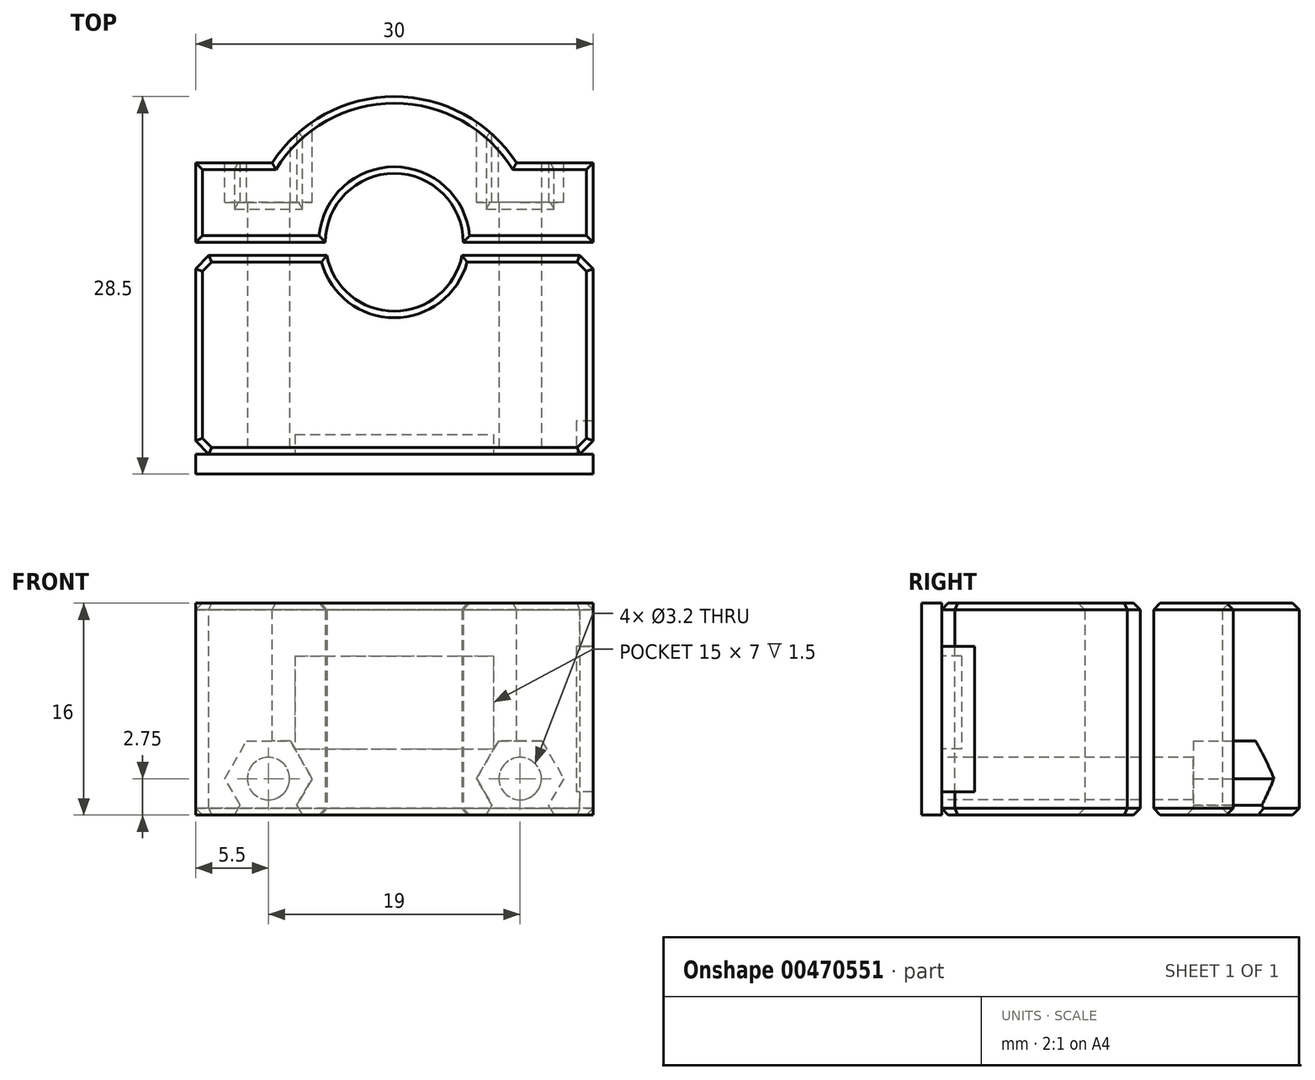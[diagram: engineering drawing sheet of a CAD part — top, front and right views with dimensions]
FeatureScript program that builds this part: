
annotation { "Feature Type Name" : "Feature", "Feature Type Description" : "" }
export const myFeature = defineFeature(function(context is Context, id is Id, definition is map)
    precondition{}
    {
        {
            var Q0;
            Q0=qCreatedBy(makeId("Top.planeOp"),FACE);
            var sketch = newSketch(context, id + "F0", { "sketchPlane" : qUnion([Q0])});
            skCircle(sketch, "E0", {"center": v(0, 0) * mm, "radius": 5.2 * mm});
            skSolve(sketch);
        }
        {
            var Q0;
            Q0=makeQuery(id+"F0.imprint","IMPRINT",FACE,{"disambiguationData":[TD([[makeQuery(id+"F0.imprint","IMPRINT",EDGE,{"derivedFrom":sQuery(id+"F0.wireOp",EDGE,"E0")}),1.0]])]});
            extrude(context, id + "F1", {"entities" : qUnion([Q0]), "depth" : 25 * mm, "hasSecondDirection" : true, "secondDirectionOppositeDirection" : true, "secondDirectionDepth" : 25 * mm});
        }
        {
            var Q0;
            Q0=qCreatedBy(makeId("Front.planeOp"),FACE);
            cPlane(context, id + "F2", {"entities" : qUnion([Q0]), "cplaneType" : CPlaneType.OFFSET, "offset" : 16 * mm, "width" : 150 * mm, "height" : 150 * mm});
        }
        {
            var Q0;
            Q0=qCreatedBy(id+"F2.planeOp",FACE);
            var sketch = newSketch(context, id + "F3", { "sketchPlane" : qUnion([Q0])});
            skPoint(sketch, "E1", {"position": v(-9.5, 0) * mm});
            skPoint(sketch, "E2", {"position": v(9.5, 0) * mm});
            skLineSegment(sketch, "E3.bottom", {"start": v(-15, -2.75) * mm, "end": v(15, -2.75) * mm});
            skLineSegment(sketch, "E3.top", {"start": v(-15, 13.25) * mm, "end": v(15, 13.25) * mm});
            skLineSegment(sketch, "E3.left", {"start": v(-15, -2.75) * mm, "end": v(-15, 13.25) * mm});
            skLineSegment(sketch, "E3.right", {"start": v(15, -2.75) * mm, "end": v(15, 13.25) * mm});
            skSolve(sketch);
        }
        {
            var Q0;
            Q0=makeQuery(id+"F3.imprint","IMPRINT",FACE,{"disambiguationData":[TD([[makeQuery(id+"F3.imprint","IMPRINT",EDGE,{"derivedFrom":sQuery(id+"F3.wireOp",EDGE,"E3.bottom")}),1.0]])]});
            extrude(context, id + "F4", {"entities" : qUnion([Q0]), "oppositeDirection" : true, "depth" : 27 * mm});
        }
        {
            var Q0;
            Q0=makeQuery(id+"F3.imprint","IMPRINT",FACE,{"disambiguationData":[TD([[makeQuery(id+"F3.imprint","IMPRINT",EDGE,{"derivedFrom":sQuery(id+"F3.wireOp",EDGE,"E3.bottom")}),1.0]])]});
            extrude(context, id + "F5", {"entities" : qUnion([Q0]), "depth" : 1.5 * mm});
        }
        {
            var Q0;
            Q0=sQuery(id+"F3.wireOp",VERTEX,"E1");
            var Q1;
            Q1=sQuery(id+"F3.wireOp",VERTEX,"E2");
            var Q2;
            Q2=makeQuery(id+"F4.opExtrude","SWEPT_BODY",BODY,{"disambiguationData":[OSD([sQuery(id+"F3.wireOp",EDGE,"E3.bottom"),sQuery(id+"F3.wireOp",EDGE,"E3.top"),sQuery(id+"F3.wireOp",EDGE,"E3.left"),sQuery(id+"F3.wireOp",EDGE,"E3.right")])]});
            hole(context, id + "F6", {"style" : HoleStyle.SIMPLE, "endStyle" : HoleEndStyle.BLIND, "holeDiameter" : 3.2 * mm, "holeDepth" : (25 - 1.5) * mm, "isTappedThrough" : true, "tappedDepth" : 15 * mm, "tapClearance" : 0, "locations" : qUnion([Q0, Q1]), "scope" : qUnion([Q2])});
        }
        {
            var Q0;
            Q0=makeQuery(id+"F4.opExtrude","CAP_FACE",FACE,{"disambiguationData":[OSD([sQuery(id+"F3.wireOp",EDGE,"E3.bottom"),sQuery(id+"F3.wireOp",EDGE,"E3.top"),sQuery(id+"F3.wireOp",EDGE,"E3.left"),sQuery(id+"F3.wireOp",EDGE,"E3.right")])],"isStart":false});
            var sketch = newSketch(context, id + "F7", { "sketchPlane" : qUnion([Q0])});
            skCircle(sketch, "E4.cCircle", {"center": v(-9.5, 0) * mm, "radius": 2.85 * mm, "construction": true});
            skLineSegment(sketch, "E4.0", {"start": v(-6.2, 0) * mm, "end": v(-7.85, -2.85) * mm});
            skLineSegment(sketch, "E4.1", {"start": v(-7.85, -2.85) * mm, "end": v(-11.15, -2.85) * mm});
            skLineSegment(sketch, "E4.2", {"start": v(-11.15, -2.85) * mm, "end": v(-12.8, 0) * mm});
            skLineSegment(sketch, "E4.3", {"start": v(-12.8, 0) * mm, "end": v(-11.15, 2.85) * mm});
            skLineSegment(sketch, "E4.4", {"start": v(-11.15, 2.85) * mm, "end": v(-7.85, 2.85) * mm});
            skLineSegment(sketch, "E4.5", {"start": v(-7.85, 2.85) * mm, "end": v(-6.2, 0) * mm});
            skPoint(sketch, "E4.0.midPoint", {"position": v(-7.03, -1.43) * mm});
            skLineSegment(sketch, "E5.MirrorCS", {"start": v(11.15, 2.85) * mm, "end": v(7.85, 2.85) * mm});
            skLineSegment(sketch, "E6.MirrorCS", {"start": v(6.2, 0) * mm, "end": v(7.85, -2.85) * mm});
            skLineSegment(sketch, "E7.MirrorCS", {"start": v(7.85, 2.85) * mm, "end": v(6.2, 0) * mm});
            skLineSegment(sketch, "E8.MirrorCS", {"start": v(12.8, 0) * mm, "end": v(11.15, 2.85) * mm});
            skLineSegment(sketch, "E9.MirrorCS", {"start": v(11.15, -2.85) * mm, "end": v(12.8, 0) * mm});
            skLineSegment(sketch, "E10.MirrorCS", {"start": v(7.85, -2.85) * mm, "end": v(11.15, -2.85) * mm});
            skCircle(sketch, "E11.MirrorC", {"center": v(9.5, 0) * mm, "radius": 2.85 * mm, "construction": true});
            skPoint(sketch, "E12.MirrorP", {"position": v(7.03, -1.43) * mm});
            skSolve(sketch);
        }
        {
            var Q0;
            Q0=makeQuery(id+"F7.imprint","IMPRINT",FACE,{"disambiguationData":[TD([[makeQuery(id+"F7.imprint","IMPRINT",EDGE,{"derivedFrom":sQuery(id+"F7.wireOp",EDGE,"E4.0")}),-1.0]])]});
            var Q1;
            Q1=makeQuery(id+"F7.imprint","IMPRINT",FACE,{"disambiguationData":[TD([[makeQuery(id+"F7.imprint","IMPRINT",EDGE,{"derivedFrom":sQuery(id+"F7.wireOp",EDGE,"E5.MirrorCS")}),1.0]])]});
            var Q2;
            {var subQ0=sQuery(id+"F7.wireOp",EDGE,"E4.3");Q2=makeQuery(id+"F7.imprint","IMPRINT",FACE,{"disambiguationData":[TD([[makeQuery(id+"F7.imprint","IMPRINT",EDGE,{"derivedFrom":subQ0}),-1.0]])]});}
            extrude(context, id + "F8", {"entities" : qUnion([Q0, Q1, Q2]), "operationType" : NewBodyOperationType.REMOVE, "oppositeDirection" : true, "depth" : 8 * mm});
        }
        {
            var Q0;
            Q0=makeQuery(id+"F4.opExtrude","SWEPT_FACE",FACE,{"disambiguationData":[OSD([sQuery(id+"F3.wireOp",EDGE,"E3.top")])]});
            var sketch = newSketch(context, id + "F9", { "sketchPlane" : qUnion([Q0])});
            skArc(sketch, "E13.0", {"start": v(9.22, 6) * mm, "mid": v(0, 11) * mm, "end": v(-9.22, 6) * mm});
            skLineSegment(sketch, "E14", {"start": v(-15, 6) * mm, "end": v(-9.22, 6) * mm});
            skPoint(sketch, "E15.orphan", {"position": v(15, 0) * mm});
            skPoint(sketch, "E16.end.orphan", {"position": v(-15, 0) * mm});
            skLineSegment(sketch, "E17.MirrorCS", {"start": v(15, 6) * mm, "end": v(9.22, 6) * mm});
            skSolve(sketch);
        }
        {
            var Q0;
            {var subQ0=sQuery(id+"F9.wireOp",EDGE,"E14");Q0=makeQuery(id+"F9.imprint","IMPRINT",FACE,{"disambiguationData":[TD([[makeQuery(id+"F9.imprint","IMPRINT",EDGE,{"derivedFrom":subQ0}),1.0]])]});}
            var Q1;
            {var subQ0=sQuery(id+"F9.wireOp",EDGE,"E17.MirrorCS");Q1=makeQuery(id+"F9.imprint","IMPRINT",FACE,{"disambiguationData":[TD([[makeQuery(id+"F9.imprint","IMPRINT",EDGE,{"derivedFrom":subQ0}),-1.0]])]});}
            extrude(context, id + "F10", {"entities" : qUnion([Q0, Q1]), "operationType" : NewBodyOperationType.REMOVE, "oppositeDirection" : true, "depth" : 25 * mm});
        }
        {
            var Q0;
            Q0=makeQuery(id+"F4.opExtrude","SWEPT_FACE",FACE,{"disambiguationData":[OSD([sQuery(id+"F3.wireOp",EDGE,"E3.top")])]});
            var sketch = newSketch(context, id + "F11", { "sketchPlane" : qUnion([Q0])});
            skLineSegment(sketch, "E18.bottom", {"start": v(-15.68, 0) * mm, "end": v(17.28, 0) * mm});
            skLineSegment(sketch, "E18.top", {"start": v(-15.68, -1) * mm, "end": v(17.28, -1) * mm});
            skLineSegment(sketch, "E18.left", {"start": v(-15.68, 0) * mm, "end": v(-15.68, -1) * mm});
            skLineSegment(sketch, "E18.right", {"start": v(17.28, 0) * mm, "end": v(17.28, -1) * mm});
            skSolve(sketch);
        }
        {
            var Q0;
            {var subQ0=sQuery(id+"F11.wireOp",EDGE,"E18.bottom");var subQ1=sQuery(id+"F3.wireOp",EDGE,"E3.top");var subQ2=makeQuery(id+"F4.opExtrude","SWEPT_EDGE",EDGE,{"disambiguationData":[OSD([subQ1,sQuery(id+"F3.wireOp",EDGE,"E3.left")])]});var subQ3=makeQuery(id+"F11.imprint","INTERSECT",VERTEX,{"derivedFrom":[subQ2,subQ0]});Q0=makeQuery(id+"F11.imprint","IMPRINT",FACE,{"disambiguationData":[TD([[makeQuery(id+"F11.imprint","IMPRINT",EDGE,{"disambiguationData":[TD([[subQ3,-1.0]])],"derivedFrom":subQ0}),-1.0]])]});}
            extrude(context, id + "F12", {"entities" : qUnion([Q0]), "operationType" : NewBodyOperationType.REMOVE, "oppositeDirection" : true, "depth" : 25 * mm});
        }
        {
            var Q0;
            Q0=makeQuery(id+"F3.imprint","IMPRINT",FACE,{"disambiguationData":[TD([[makeQuery(id+"F3.imprint","IMPRINT",EDGE,{"derivedFrom":sQuery(id+"F3.wireOp",EDGE,"E3.bottom")}),1.0]])]});
            var sketch = newSketch(context, id + "F13", { "sketchPlane" : qUnion([Q0])});
            skLineSegment(sketch, "E19.bottom", {"start": v(-7.5, 9.25) * mm, "end": v(7.5, 9.25) * mm});
            skLineSegment(sketch, "E19.top", {"start": v(-7.5, 2.25) * mm, "end": v(7.5, 2.25) * mm});
            skLineSegment(sketch, "E19.left", {"start": v(-7.5, 9.25) * mm, "end": v(-7.5, 2.25) * mm});
            skLineSegment(sketch, "E19.right", {"start": v(7.5, 9.25) * mm, "end": v(7.5, 2.25) * mm});
            skSolve(sketch);
        }
        {
            var Q0;
            Q0=makeQuery(id+"F13.imprint","IMPRINT",FACE,{"disambiguationData":[TD([[makeQuery(id+"F13.imprint","IMPRINT",EDGE,{"derivedFrom":sQuery(id+"F13.wireOp",EDGE,"E19.bottom")}),-1.0]])]});
            extrude(context, id + "F14", {"entities" : qUnion([Q0]), "operationType" : NewBodyOperationType.REMOVE, "oppositeDirection" : true, "depth" : 1.5 * mm});
        }
        {
            var Q0;
            Q0=makeQuery(id+"F3.imprint","IMPRINT",FACE,{"disambiguationData":[TD([[makeQuery(id+"F3.imprint","IMPRINT",EDGE,{"derivedFrom":sQuery(id+"F3.wireOp",EDGE,"E3.bottom")}),1.0]])]});
            var sketch = newSketch(context, id + "F15", { "sketchPlane" : qUnion([Q0])});
            skLineSegment(sketch, "E20.bottom", {"start": v(18.98, 10) * mm, "end": v(13.75, 10) * mm});
            skLineSegment(sketch, "E20.top", {"start": v(18.98, -1) * mm, "end": v(13.75, -1) * mm});
            skLineSegment(sketch, "E20.left", {"start": v(18.98, 10) * mm, "end": v(18.98, -1) * mm});
            skLineSegment(sketch, "E20.right", {"start": v(13.75, 10) * mm, "end": v(13.75, -1) * mm});
            skSolve(sketch);
        }
        {
            var Q0;
            {var subQ0=sQuery(id+"F15.wireOp",EDGE,"E20.right");Q0=makeQuery(id+"F15.imprint","IMPRINT",FACE,{"disambiguationData":[TD([[makeQuery(id+"F15.imprint","IMPRINT",EDGE,{"derivedFrom":subQ0}),1.0]])]});}
            extrude(context, id + "F16", {"entities" : qUnion([Q0]), "operationType" : NewBodyOperationType.REMOVE, "oppositeDirection" : true, "depth" : 2.5 * mm});
        }
        {
            var Q0;
            Q0=makeQuery(id+"F1.opExtrude","SWEPT_BODY",BODY,{"disambiguationData":[OSD([sQuery(id+"F0.wireOp",EDGE,"E0")])]});
            var Q1;
            Q1=makeQuery(id+"F12.boolean.opBoolean","SPLIT",BODY,{"disambiguationData":[OD(1.0)],"derivedFrom":makeQuery(id+"F4.opExtrude","SWEPT_BODY",BODY,{"disambiguationData":[OSD([sQuery(id+"F3.wireOp",EDGE,"E3.bottom"),sQuery(id+"F3.wireOp",EDGE,"E3.top"),sQuery(id+"F3.wireOp",EDGE,"E3.left"),sQuery(id+"F3.wireOp",EDGE,"E3.right")])]})});
            var Q2;
            Q2=makeQuery(id+"F12.boolean.opBoolean","SPLIT",BODY,{"disambiguationData":[OD(0.0)],"derivedFrom":makeQuery(id+"F4.opExtrude","SWEPT_BODY",BODY,{"disambiguationData":[OSD([sQuery(id+"F3.wireOp",EDGE,"E3.bottom"),sQuery(id+"F3.wireOp",EDGE,"E3.top"),sQuery(id+"F3.wireOp",EDGE,"E3.left"),sQuery(id+"F3.wireOp",EDGE,"E3.right")])]})});
            booleanBodies(context, id + "F17", {"operationType" : BooleanOperationType.SUBTRACTION, "tools" : qUnion([Q0]), "targets" : qUnion([Q1, Q2])});
        }
        {
            var Q0;
            Q0=makeQuery(id+"F4.opExtrude","CAP_EDGE",EDGE,{"disambiguationData":[OSD([sQuery(id+"F3.wireOp",EDGE,"E3.left")])],"isStart":true});
            var Q1;
            {var subQ0=sQuery(id+"F3.wireOp",EDGE,"E3.right");var subQ1=sQuery(id+"F3.wireOp",EDGE,"E3.top");Q1=makeQuery(id+"F16.boolean.opBoolean","SPLIT",EDGE,{"disambiguationData":[TD([makeQuery(id+"F4.opExtrude","SWEPT_FACE",FACE,{"disambiguationData":[OSD([subQ1])]})])],"derivedFrom":makeQuery(id+"F4.opExtrude","CAP_EDGE",EDGE,{"disambiguationData":[OSD([subQ0])],"isStart":true})});}
            var Q2;
            {var subQ0=sQuery(id+"F3.wireOp",EDGE,"E3.bottom");var subQ1=sQuery(id+"F3.wireOp",EDGE,"E3.right");Q2=makeQuery(id+"F16.boolean.opBoolean","SPLIT",EDGE,{"disambiguationData":[TD([makeQuery(id+"F4.opExtrude","SWEPT_FACE",FACE,{"disambiguationData":[OSD([subQ0])]})])],"derivedFrom":makeQuery(id+"F4.opExtrude","CAP_EDGE",EDGE,{"disambiguationData":[OSD([subQ1])],"isStart":true})});}
            var Q3;
            Q3=makeQuery(id+"F12.boolean.opBoolean","COPY",EDGE,{"derivedFrom":makeQuery(id+"F12.opExtrude","SWEPT_EDGE",EDGE,{"disambiguationData":[OSD([sQuery(id+"F3.wireOp",EDGE,"E3.top"),sQuery(id+"F3.wireOp",EDGE,"E3.right"),sQuery(id+"F11.wireOp",EDGE,"E18.top")])]})});
            var Q4;
            Q4=makeQuery(id+"F12.boolean.opBoolean","COPY",EDGE,{"derivedFrom":makeQuery(id+"F12.opExtrude","SWEPT_EDGE",EDGE,{"disambiguationData":[OSD([sQuery(id+"F3.wireOp",EDGE,"E3.top"),sQuery(id+"F3.wireOp",EDGE,"E3.right"),sQuery(id+"F11.wireOp",EDGE,"E18.bottom")])]})});
            var Q5;
            Q5=makeQuery(id+"F10.boolean.opBoolean","COPY",EDGE,{"derivedFrom":makeQuery(id+"F10.opExtrude","SWEPT_EDGE",EDGE,{"disambiguationData":[OSD([sQuery(id+"F3.wireOp",EDGE,"E3.top"),sQuery(id+"F3.wireOp",EDGE,"E3.right"),sQuery(id+"F9.wireOp",EDGE,"E17.MirrorCS")])]})});
            var Q6;
            Q6=makeQuery(id+"F12.boolean.opBoolean","COPY",EDGE,{"derivedFrom":makeQuery(id+"F12.opExtrude","SWEPT_EDGE",EDGE,{"disambiguationData":[OSD([sQuery(id+"F3.wireOp",EDGE,"E3.top"),sQuery(id+"F3.wireOp",EDGE,"E3.left"),sQuery(id+"F11.wireOp",EDGE,"E18.top")])]})});
            var Q7;
            Q7=makeQuery(id+"F12.boolean.opBoolean","COPY",EDGE,{"derivedFrom":makeQuery(id+"F12.opExtrude","SWEPT_EDGE",EDGE,{"disambiguationData":[OSD([sQuery(id+"F3.wireOp",EDGE,"E3.top"),sQuery(id+"F3.wireOp",EDGE,"E3.left"),sQuery(id+"F11.wireOp",EDGE,"E18.bottom")])]})});
            var Q8;
            Q8=makeQuery(id+"F10.boolean.opBoolean","COPY",EDGE,{"derivedFrom":makeQuery(id+"F10.opExtrude","SWEPT_EDGE",EDGE,{"disambiguationData":[OSD([sQuery(id+"F3.wireOp",EDGE,"E3.top"),sQuery(id+"F3.wireOp",EDGE,"E3.left"),sQuery(id+"F9.wireOp",EDGE,"E14")])]})});
            chamfer(context, id + "F18", {"entities" : qUnion([Q0, Q1, Q2, Q3, Q4, Q5, Q6, Q7, Q8]), "width" : 1 * mm, "tangentPropagation" : true});
        }
        {
            var Q0;
            {var subQ6=sQuery(id+"F3.wireOp",EDGE,"E3.bottom");var subQ8=sQuery(id+"F7.wireOp",EDGE,"E4.0");Q0=makeQuery(id+"F12.boolean.opBoolean","SPLIT",FACE,{"disambiguationData":[TD([makeQuery(id+"F8.boolean.opBoolean","COPY",FACE,{"derivedFrom":makeQuery(id+"F8.opExtrude","SWEPT_FACE",FACE,{"disambiguationData":[OSD([subQ8])]})})])],"derivedFrom":makeQuery(id+"F4.opExtrude","SWEPT_FACE",FACE,{"disambiguationData":[OSD([subQ6])]})});}
            var Q1;
            {var subQ2=sQuery(id+"F3.wireOp",EDGE,"E3.bottom");Q1=makeQuery(id+"F12.boolean.opBoolean","SPLIT",FACE,{"disambiguationData":[TD([makeQuery(id+"F12.opExtrude","SWEPT_FACE",FACE,{"disambiguationData":[OSD([sQuery(id+"F11.wireOp",EDGE,"E18.top")])]})])],"derivedFrom":makeQuery(id+"F4.opExtrude","SWEPT_FACE",FACE,{"disambiguationData":[OSD([subQ2])]})});}
            var Q2;
            {var subQ0=sQuery(id+"F9.wireOp",EDGE,"E14");var subQ2=sQuery(id+"F3.wireOp",EDGE,"E3.top");Q2=makeQuery(id+"F12.boolean.opBoolean","SPLIT",FACE,{"disambiguationData":[TD([makeQuery(id+"F10.boolean.opBoolean","COPY",FACE,{"derivedFrom":makeQuery(id+"F10.opExtrude","SWEPT_FACE",FACE,{"disambiguationData":[OSD([subQ0])]})})])],"derivedFrom":makeQuery(id+"F4.opExtrude","SWEPT_FACE",FACE,{"disambiguationData":[OSD([subQ2])]})});}
            var Q3;
            {var subQ2=sQuery(id+"F3.wireOp",EDGE,"E3.top");Q3=makeQuery(id+"F12.boolean.opBoolean","SPLIT",FACE,{"disambiguationData":[TD([makeQuery(id+"F12.opExtrude","SWEPT_FACE",FACE,{"disambiguationData":[OSD([sQuery(id+"F11.wireOp",EDGE,"E18.top")])]})])],"derivedFrom":makeQuery(id+"F4.opExtrude","SWEPT_FACE",FACE,{"disambiguationData":[OSD([subQ2])]})});}
            chamfer(context, id + "F19", {"entities" : qUnion([Q0, Q1, Q2, Q3]), "width" : .5 * mm, "tangentPropagation" : true});
        }
    });
